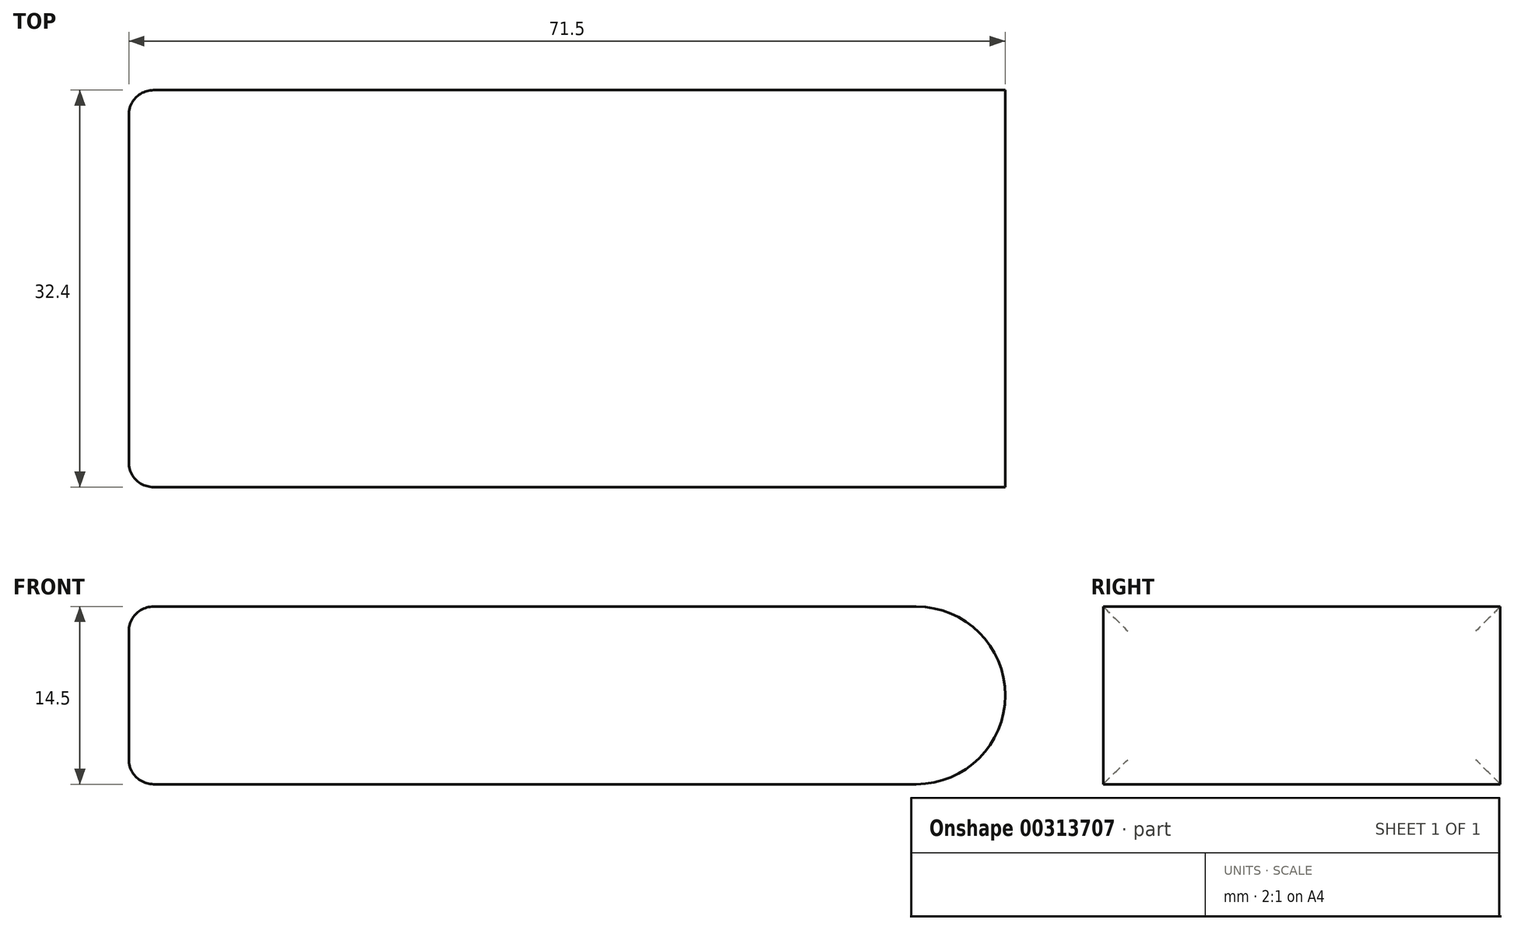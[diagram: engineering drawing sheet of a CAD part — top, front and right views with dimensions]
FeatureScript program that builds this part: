
annotation { "Feature Type Name" : "Feature", "Feature Type Description" : "" }
export const myFeature = defineFeature(function(context is Context, id is Id, definition is map)
    precondition{}
    {
        {
            var Q0;
            Q0=qCreatedBy(makeId("Top.planeOp"),FACE);
            var sketch = newSketch(context, id + "F0", { "sketchPlane" : qUnion([Q0])});
            skLineSegment(sketch, "E0.bottom", {"start": v(-35.75, 16.2) * mm, "end": v(35.75, 16.2) * mm});
            skLineSegment(sketch, "E0.top", {"start": v(-35.75, -16.2) * mm, "end": v(35.75, -16.2) * mm});
            skLineSegment(sketch, "E0.left", {"start": v(-35.75, 16.2) * mm, "end": v(-35.75, -16.2) * mm});
            skLineSegment(sketch, "E0.right", {"start": v(35.75, 16.2) * mm, "end": v(35.75, -16.2) * mm});
            skPoint(sketch, "E0.middle", {"position": v(0, 0) * mm});
            skSolve(sketch);
        }
        {
            var Q0;
            Q0=qSketchRegion(id+"F0",true);
            extrude(context, id + "F1", {"entities" : qUnion([Q0]), "depth" : 14.5 * mm});
        }
        {
            var Q0;
            Q0=makeQuery(id+"F1.opExtrude","SWEPT_FACE",FACE,{"disambiguationData":[OSD([sQuery(id+"F0.wireOp",EDGE,"E0.left")])]});
            fillet(context, id + "F2", {"entities" : qUnion([Q0]), "radius" : 2 * mm, "tangentPropagation" : true, "allowEdgeOverflow" : false});
        }
        {
            var Q0;
            Q0=makeQuery(id+"F1.opExtrude","CAP_EDGE",EDGE,{"disambiguationData":[OSD([sQuery(id+"F0.wireOp",EDGE,"E0.right")])],"isStart":false});
            var Q1;
            Q1=makeQuery(id+"F1.opExtrude","CAP_EDGE",EDGE,{"disambiguationData":[OSD([sQuery(id+"F0.wireOp",EDGE,"E0.right")])],"isStart":true});
            fillet(context, id + "F3", {"entities" : qUnion([Q0, Q1]), "radius" : 7.25 * mm, "tangentPropagation" : true, "allowEdgeOverflow" : false});
        }
    });
